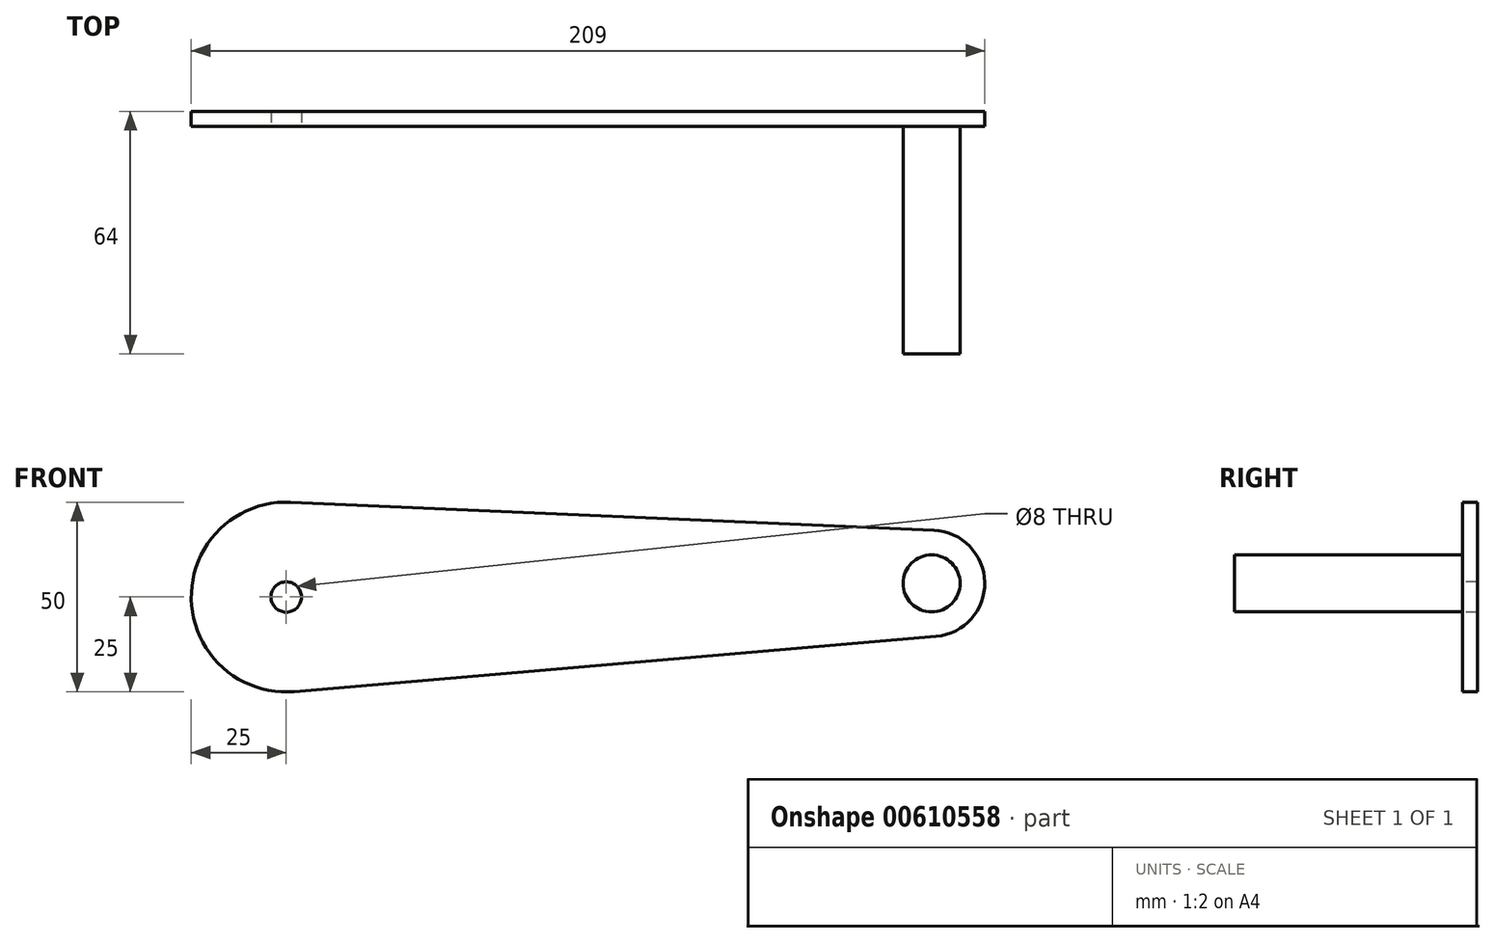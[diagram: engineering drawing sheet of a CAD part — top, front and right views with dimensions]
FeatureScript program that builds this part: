
annotation { "Feature Type Name" : "Feature", "Feature Type Description" : "" }
export const myFeature = defineFeature(function(context is Context, id is Id, definition is map)
    precondition{}
    {
        {
            var Q0;
            Q0=qCreatedBy(makeId("Front.planeOp"),FACE);
            var sketch = newSketch(context, id + "F0", { "sketchPlane" : qUnion([Q0])});
            skCircle(sketch, "E0", {"center": v(0, 0) * mm, "radius": 25 * mm});
            skCircle(sketch, "E1", {"center": v(0, 0) * mm, "radius": 4 * mm});
            skCircle(sketch, "E2", {"center": v(170, 3.59) * mm, "radius": 14 * mm});
            skCircle(sketch, "E3", {"center": v(170, 3.59) * mm, "radius": 7.5 * mm});
            skLineSegment(sketch, "E4", {"start": v(1.1, 24.98) * mm, "end": v(170.61, 17.57) * mm});
            skLineSegment(sketch, "E5", {"start": v(171.2, -10.36) * mm, "end": v(2.14, -24.9) * mm});
            skSolve(sketch);
        }
        {
            var Q0;
            Q0 = qSketchRegion(id + "F0", true);
            var Q1;
            Q1=makeQuery(id+"F0.imprint","IMPRINT",FACE,{"disambiguationData":[TD([[makeQuery(id+"F0.imprint","IMPRINT",EDGE,{"derivedFrom":sQuery(id+"F0.wireOp",EDGE,"E3")}),1.0]])]});
            extrude(context, id + "F1", {"entities" : qUnion([Q0, Q1]), "oppositeDirection" : true, "depth" : 4 * mm, "offsetDistance" : 25 * mm});
        }
        {
            var Q0;
            Q0=makeQuery(id+"F0.imprint","IMPRINT",FACE,{"disambiguationData":[TD([[makeQuery(id+"F0.imprint","IMPRINT",EDGE,{"derivedFrom":sQuery(id+"F0.wireOp",EDGE,"E3")}),1.0]])]});
            extrude(context, id + "F2", {"entities" : qUnion([Q0]), "operationType" : NewBodyOperationType.ADD, "depth" : 60 * mm, "offsetDistance" : 25 * mm});
        }
    });
